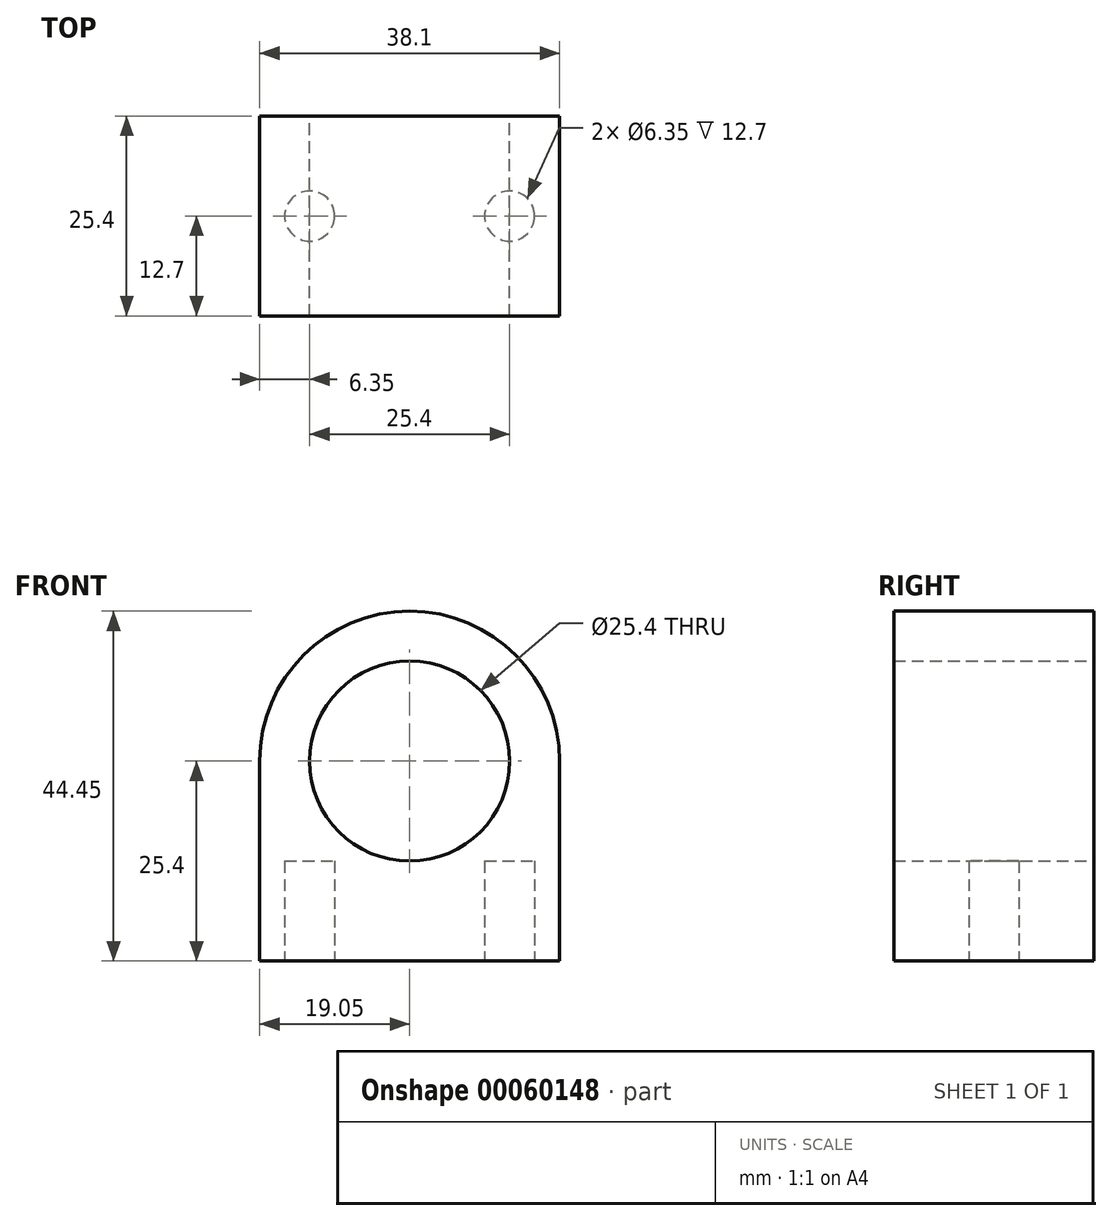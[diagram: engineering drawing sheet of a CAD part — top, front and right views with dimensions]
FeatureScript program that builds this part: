
annotation { "Feature Type Name" : "Feature", "Feature Type Description" : "" }
export const myFeature = defineFeature(function(context is Context, id is Id, definition is map)
    precondition{}
    {
        {
            var Q0;
            Q0=qCreatedBy(makeId("Front.planeOp"),FACE);
            var sketch = newSketch(context, id + "F0", { "sketchPlane" : qUnion([Q0])});
            skCircle(sketch, "E0", {"center": v(0, 0) * mm, "radius": 19.05 * mm});
            skLineSegment(sketch, "E1.bottom", {"start": v(-19.05, 0) * mm, "end": v(19.05, 0) * mm});
            skLineSegment(sketch, "E1.top", {"start": v(-19.05, -25.4) * mm, "end": v(19.05, -25.4) * mm});
            skLineSegment(sketch, "E1.left", {"start": v(-19.05, 0) * mm, "end": v(-19.05, -25.4) * mm});
            skLineSegment(sketch, "E1.right", {"start": v(19.05, 0) * mm, "end": v(19.05, -25.4) * mm});
            skCircle(sketch, "E2", {"center": v(0, 0) * mm, "radius": 12.7 * mm});
            skSolve(sketch);
        }
        {
            var Q0;
            Q0=makeQuery(id+"F0.imprint","IMPRINT",FACE,{"disambiguationData":[TD([[makeQuery(id+"F0.imprint","IMPRINT",EDGE,{"derivedFrom":sQuery(id+"F0.wireOp",EDGE,"E1.top")}),1.0]])]});
            var Q1;
            {var subQ0=sQuery(id+"F0.wireOp",EDGE,"E1.bottom");var subQ4=sQuery(id+"F0.wireOp",EDGE,"E2");var subQ5=makeQuery(id+"F0.imprint","INTERSECT",VERTEX,{"disambiguationData":[OD(0.0)],"derivedFrom":[subQ0,subQ4]});Q1=makeQuery(id+"F0.imprint","IMPRINT",FACE,{"disambiguationData":[TD([[makeQuery(id+"F0.imprint","IMPRINT",EDGE,{"disambiguationData":[TD([[subQ5,-1.0]])],"derivedFrom":subQ4}),-1.0]])]});}
            var Q2;
            {var subQ0=sQuery(id+"F0.wireOp",EDGE,"E1.bottom");var subQ4=sQuery(id+"F0.wireOp",EDGE,"E2");var subQ5=makeQuery(id+"F0.imprint","INTERSECT",VERTEX,{"disambiguationData":[OD(0.0)],"derivedFrom":[subQ0,subQ4]});Q2=makeQuery(id+"F0.imprint","IMPRINT",FACE,{"disambiguationData":[TD([[makeQuery(id+"F0.imprint","IMPRINT",EDGE,{"disambiguationData":[TD([[subQ5,1.0]])],"derivedFrom":subQ4}),-1.0]])]});}
            extrude(context, id + "F1", {"entities" : qUnion([Q0, Q1, Q2]), "endBound" : BoundingType.SYMMETRIC, "depth" : 25.4 * mm});
        }
        {
            var Q0;
            Q0=makeQuery(id+"F1.opExtrude","SWEPT_FACE",FACE,{"disambiguationData":[OSD([sQuery(id+"F0.wireOp",EDGE,"E1.top")])]});
            var sketch = newSketch(context, id + "F2", { "sketchPlane" : qUnion([Q0])});
            skCircle(sketch, "E3", {"center": v(-12.7, 0) * mm, "radius": 3.18 * mm});
            skCircle(sketch, "E4", {"center": v(12.7, 0) * mm, "radius": 3.18 * mm});
            skSolve(sketch);
        }
        {
            var Q0;
            Q0 = qSketchRegion(id + "F2", true);
            extrude(context, id + "F3", {"entities" : qUnion([Q0]), "operationType" : NewBodyOperationType.REMOVE, "oppositeDirection" : true, "depth" : 12.7 * mm});
        }
    });
